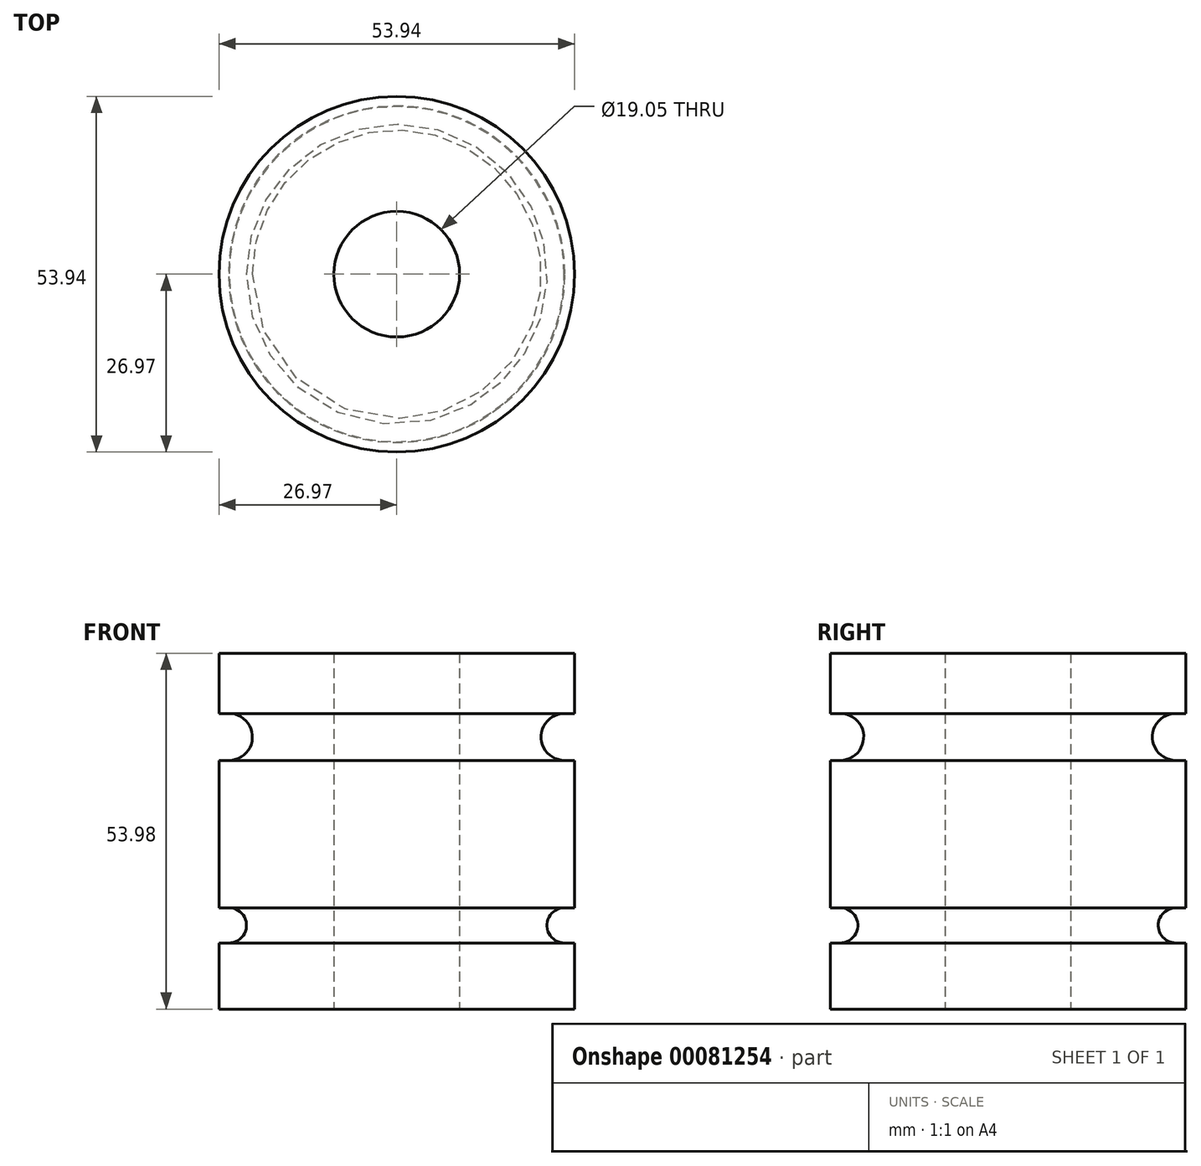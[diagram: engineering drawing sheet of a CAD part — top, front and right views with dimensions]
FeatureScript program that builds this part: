
annotation { "Feature Type Name" : "Feature", "Feature Type Description" : "" }
export const myFeature = defineFeature(function(context is Context, id is Id, definition is map)
    precondition{}
    {
        {
            var Q0;
            Q0=qCreatedBy(makeId("Front.planeOp"),FACE);
            var sketch = newSketch(context, id + "F0", { "sketchPlane" : qUnion([Q0])});
            skLineSegment(sketch, "E0", {"start": v(0, 0) * mm, "end": v(0, 34.1) * mm, "construction": true});
            skLineSegment(sketch, "E1", {"start": v(-9.53, 0) * mm, "end": v(-9.53, 53.98) * mm});
            skLineSegment(sketch, "E2", {"start": v(-9.53, 53.98) * mm, "end": v(-26.97, 53.98) * mm});
            skLineSegment(sketch, "E3", {"start": v(-26.97, 0) * mm, "end": v(-9.53, 0) * mm});
            skLineSegment(sketch, "E4", {"start": v(-26.97, 53.98) * mm, "end": v(-26.97, 44.83) * mm});
            skArc(sketch, "E5", {"start": v(-25.45, 10.03) * mm, "mid": v(-22.78, 12.7) * mm, "end": v(-25.45, 15.37) * mm});
            skArc(sketch, "E6", {"start": v(-25.5, 37.72) * mm, "mid": v(-21.9, 41.29) * mm, "end": v(-25.52, 44.83) * mm});
            skLineSegment(sketch, "E7", {"start": v(-25.45, 15.37) * mm, "end": v(-26.97, 15.37) * mm});
            skLineSegment(sketch, "E8", {"start": v(-25.52, 44.83) * mm, "end": v(-26.97, 44.83) * mm});
            skLineSegment(sketch, "E9", {"start": v(-25.4, 37.72) * mm, "end": v(-26.97, 37.72) * mm});
            skLineSegment(sketch, "E10.trimOffspring", {"start": v(-26.97, 37.72) * mm, "end": v(-26.97, 15.37) * mm});
            skLineSegment(sketch, "E11.trimOffspring", {"start": v(-26.97, 10.04) * mm, "end": v(-26.97, 0) * mm});
            skLineSegment(sketch, "E12", {"start": v(-25.45, 10.03) * mm, "end": v(-26.97, 10.03) * mm});
            skSolve(sketch);
        }
        {
            var Q0;
            Q0 = qSketchRegion(id + "F0", true);
            var Q1;
            Q1=sQuery(id+"F0.wireOp",EDGE,"E0");
            revolve(context, id + "F1", {"entities" : qUnion([Q0]), "axis" : qUnion([Q1]), "revolveType" : RevolveType.FULL});
        }
    });
